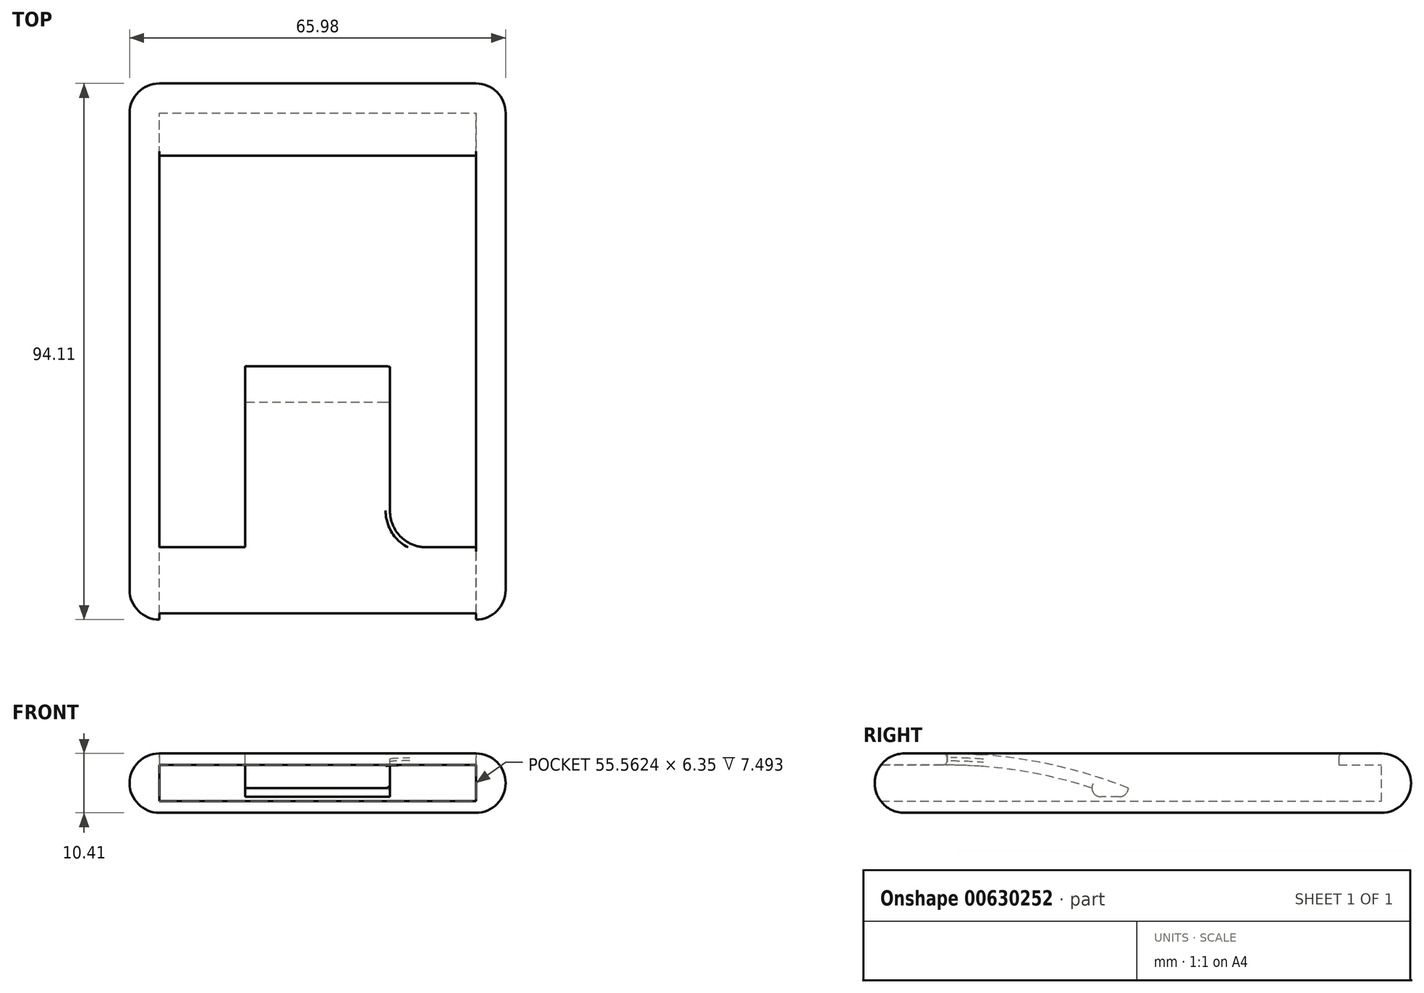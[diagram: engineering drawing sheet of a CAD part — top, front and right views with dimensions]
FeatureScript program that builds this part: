
annotation { "Feature Type Name" : "Feature", "Feature Type Description" : "" }
export const myFeature = defineFeature(function(context is Context, id is Id, definition is map)
    precondition{}
    {
        {
            var Q0;
            Q0=qCreatedBy(makeId("Front.planeOp"),FACE);
            var sketch = newSketch(context, id + "F0", { "sketchPlane" : qUnion([Q0])});
            skLineSegment(sketch, "E0.top", {"start": v(-27.78, 0) * mm, "end": v(27.78, 0) * mm});
            skLineSegment(sketch, "E0.left", {"start": v(-27.78, 2.03) * mm, "end": v(-27.78, 0) * mm});
            skLineSegment(sketch, "E0.right", {"start": v(27.78, 2.03) * mm, "end": v(27.78, 0) * mm});
            skLineSegment(sketch, "E1", {"start": v(0, 0) * mm, "end": v(0, 24.78) * mm, "construction": true});
            skLineSegment(sketch, "E2", {"start": v(-27.78, 2.03) * mm, "end": v(27.78, 2.03) * mm});
            skLineSegment(sketch, "E3", {"start": v(-27.78, 0) * mm, "end": v(-27.78, 10.41) * mm});
            skArc(sketch, "E4", {"start": v(-27.78, 10.41) * mm, "mid": v(-32.99, 5.2) * mm, "end": v(-27.78, 0) * mm});
            skLineSegment(sketch, "E5.MirrorCS", {"start": v(27.78, 0) * mm, "end": v(27.78, 10.41) * mm});
            skArc(sketch, "E6.MirrorCS", {"start": v(27.78, 10.41) * mm, "mid": v(32.99, 5.2) * mm, "end": v(27.78, 0) * mm});
            skSolve(sketch);
        }
        {
            var Q0;
            Q0 = qSketchRegion(id + "F0", true);
            extrude(context, id + "F1", {"entities" : qUnion([Q0]), "endBound" : BoundingType.SYMMETRIC, "depth" : 88.9 * mm, "offsetDistance" : 25.4 * mm});
        }
        {
            var Q0;
            Q0=makeQuery(id+"F1.opExtrude","CAP_FACE",FACE,{"disambiguationData":[OSD([sQuery(id+"F0.wireOp",EDGE,"E0.top"),sQuery(id+"F0.wireOp",EDGE,"E2"),sQuery(id+"F0.wireOp",EDGE,"E3"),sQuery(id+"F0.wireOp",EDGE,"E4"),sQuery(id+"F0.wireOp",EDGE,"E5.MirrorCS"),sQuery(id+"F0.wireOp",EDGE,"E6.MirrorCS")])],"isStart":true});
            var sketch = newSketch(context, id + "F2", { "sketchPlane" : qUnion([Q0])});
            skLineSegment(sketch, "E7", {"start": v(-27.78, 10.41) * mm, "end": v(27.78, 10.41) * mm});
            skSolve(sketch);
        }
        {
            var Q0;
            Q0 = qSketchRegion(id + "F2", true);
            var Q1;
            Q1=makeQuery(id+"F2.imprint","IMPRINT",FACE,{"disambiguationData":[TD([[makeQuery(id+"F2.imprint","IMPRINT",EDGE,{"derivedFrom":sQuery(id+"F2.wireOp",EDGE,"E7")}),-1.0]])]});
            var Q2;
            Q2=makeQuery(id+"F2.imprint","IMPRINT",FACE,{"disambiguationData":[TD([[makeQuery(id+"F2.imprint","IMPRINT",EDGE,{"derivedFrom":makeQuery(id+"F1.opExtrude","CAP_EDGE",EDGE,{"disambiguationData":[OSD([sQuery(id+"F0.wireOp",EDGE,"E0.top")])],"isStart":true})}),-1.0]])]});
            extrude(context, id + "F3", {"entities" : qUnion([Q0, Q1, Q2]), "operationType" : NewBodyOperationType.ADD, "depth" : 5.2 * mm, "offsetDistance" : 25.4 * mm});
        }
        {
            var Q0;
            Q0=makeQuery(id+"F1.opExtrude","SWEPT_FACE",FACE,{"disambiguationData":[OSD([sQuery(id+"F0.wireOp",EDGE,"E3")])]});
            var sketch = newSketch(context, id + "F4", { "sketchPlane" : qUnion([Q0])});
            skLineSegment(sketch, "E8.bottom", {"start": v(-44.45, 10.41) * mm, "end": v(-31.75, 10.41) * mm});
            skLineSegment(sketch, "E8.top", {"start": v(-44.45, 8.38) * mm, "end": v(-31.75, 8.38) * mm});
            skLineSegment(sketch, "E8.left", {"start": v(-44.45, 10.41) * mm, "end": v(-44.45, 8.38) * mm});
            skLineSegment(sketch, "E8.right", {"start": v(-31.75, 10.41) * mm, "end": v(-31.75, 8.38) * mm});
            skLineSegment(sketch, "E9.0", {"start": v(44.45, 2.03) * mm, "end": v(44.45, 10.41) * mm});
            skLineSegment(sketch, "E10", {"start": v(36.96, 10.41) * mm, "end": v(36.96, 8.38) * mm});
            skLineSegment(sketch, "E11.trimOffspring", {"start": v(36.96, 10.41) * mm, "end": v(44.45, 10.41) * mm});
            skLineSegment(sketch, "E12.trimOffspring", {"start": v(36.96, 8.38) * mm, "end": v(44.45, 8.38) * mm});
            skSolve(sketch);
        }
        {
            var Q0;
            Q0=makeQuery(id+"F4.imprint","IMPRINT",FACE,{"disambiguationData":[TD([[makeQuery(id+"F4.imprint","IMPRINT",EDGE,{"derivedFrom":sQuery(id+"F4.wireOp",EDGE,"E8.bottom")}),-1.0]])]});
            var Q1;
            Q1=makeQuery(id+"F4.imprint","IMPRINT",FACE,{"disambiguationData":[TD([[makeQuery(id+"F4.imprint","IMPRINT",EDGE,{"derivedFrom":sQuery(id+"F4.wireOp",EDGE,"E10")}),1.0]])]});
            extrude(context, id + "F5", {"entities" : qUnion([Q0, Q1]), "operationType" : NewBodyOperationType.ADD, "endBound" : BoundingType.UP_TO_NEXT, "depth" : 25.4 * mm, "offsetDistance" : 25.4 * mm});
        }
        {
            var Q0;
            Q0=makeQuery(id+"F3.opExtrude","CAP_EDGE",EDGE,{"disambiguationData":[OSD([sQuery(id+"F2.wireOp",EDGE,"E7")])],"isStart":false});
            var Q1;
            Q1=makeQuery(id+"F1.opExtrude","CAP_EDGE",EDGE,{"disambiguationData":[OSD([sQuery(id+"F0.wireOp",EDGE,"E4")])],"isStart":false});
            fillet(context, id + "F6", {"entities" : qUnion([Q0, Q1]), "radius" : 5.2 * mm, "tangentPropagation" : true, "allowEdgeOverflow" : false});
        }
        {
            var Q0;
            Q0=qCreatedBy(makeId("Right.planeOp"),FACE);
            var sketch = newSketch(context, id + "F7", { "sketchPlane" : qUnion([Q0])});
            skLineSegment(sketch, "E13.0", {"start": v(-31.75, 8.38) * mm, "end": v(-43.37, 8.38) * mm});
            skLineSegment(sketch, "E13.1", {"start": v(-31.75, 8.38) * mm, "end": v(-31.75, 10.41) * mm});
            skArc(sketch, "E14", {"start": v(0, 4.35) * mm, "mid": v(-15.59, 8.88) * mm, "end": v(-31.75, 10.41) * mm});
            skLineSegment(sketch, "E15", {"start": v(-1.52, 2.83) * mm, "end": v(-4.83, 2.83) * mm});
            skLineSegment(sketch, "E16", {"start": v(0, 4.35) * mm, "end": v(0, 4.35) * mm});
            skLineSegment(sketch, "E17", {"start": v(0, 4.35) * mm, "end": v(-6.35, 4.35) * mm, "construction": true});
            skLineSegment(sketch, "E18", {"start": v(-6.35, 4.35) * mm, "end": v(-6.35, 4.35) * mm});
            skArc(sketch, "E19", {"start": v(-6.35, 4.35) * mm, "mid": v(-18.9, 7.37) * mm, "end": v(-31.75, 8.38) * mm});
            skPoint(sketch, "E20.visualSharp", {"position": v(-6.35, 2.83) * mm});
            skArc(sketch, "E20.filletArc", {"start": v(-6.35, 4.35) * mm, "mid": v(-5.9, 3.27) * mm, "end": v(-4.83, 2.83) * mm});
            skPoint(sketch, "E21.visualSharp", {"position": v(0, 2.83) * mm});
            skArc(sketch, "E21.filletArc", {"start": v(-1.52, 2.83) * mm, "mid": v(-0.45, 3.27) * mm, "end": v(0, 4.35) * mm});
            skSolve(sketch);
        }
        {
            var Q0;
            Q0 = qSketchRegion(id + "F7", true);
            extrude(context, id + "F8", {"entities" : qUnion([Q0]), "operationType" : NewBodyOperationType.ADD, "endBound" : BoundingType.SYMMETRIC, "depth" : 25.4 * mm, "offsetDistance" : 25.4 * mm});
        }
        {
            var Q0;
            Q0=makeQuery(id+"F8.opExtrude","CAP_EDGE",EDGE,{"disambiguationData":[OSD([sQuery(id+"F7.wireOp",EDGE,"E13.1")])],"isStart":true});
            var Q1;
            Q1=makeQuery(id+"F5.opExtrude","CAP_EDGE",EDGE,{"disambiguationData":[OSD([sQuery(id+"F4.wireOp",EDGE,"E8.right")])],"isStart":true});
            var Q2;
            Q2=makeQuery(id+"F8.opExtrude","CAP_EDGE",EDGE,{"disambiguationData":[OSD([sQuery(id+"F7.wireOp",EDGE,"E13.1")])],"isStart":false});
            var Q3;
            Q3=makeQuery(id+"F5.opExtrude","CAP_EDGE",EDGE,{"disambiguationData":[OSD([sQuery(id+"F4.wireOp",EDGE,"E8.right")])],"isStart":false});
            var Q4;
            Q4=makeQuery(id+"F5.opExtrude","CAP_EDGE",EDGE,{"disambiguationData":[OSD([sQuery(id+"F4.wireOp",EDGE,"E10")])],"isStart":false});
            var Q5;
            Q5=makeQuery(id+"F5.opExtrude","CAP_EDGE",EDGE,{"disambiguationData":[OSD([sQuery(id+"F4.wireOp",EDGE,"E10")])],"isStart":true});
            fillet(context, id + "F9", {"entities" : qUnion([Q0, Q1, Q2, Q3, Q4, Q5]), "radius" : 6.35 * mm, "tangentPropagation" : true, "allowEdgeOverflow" : false});
        }
        {
            var Q0;
            Q0=makeQuery(id+"F9.opFillet","BLEND_EDGE",EDGE,{"blendedFrom":[makeQuery(id+"F8.opExtrude","CAP_EDGE",EDGE,{"disambiguationData":[OSD([sQuery(id+"F7.wireOp",EDGE,"E13.1")])],"isStart":false}),makeQuery(id+"F8.opExtrude","SWEPT_FACE",FACE,{"disambiguationData":[OSD([sQuery(id+"F7.wireOp",EDGE,"E14")])]})],"blendedInto":[makeQuery(id+"F8.opExtrude","SWEPT_FACE",FACE,{"disambiguationData":[OSD([sQuery(id+"F7.wireOp",EDGE,"E14")])]})]});
            var Q1;
            Q1=makeQuery(id+"F9.opFillet","BLEND_EDGE",EDGE,{"blendedFrom":[makeQuery(id+"F8.opExtrude","CAP_EDGE",EDGE,{"disambiguationData":[OSD([sQuery(id+"F7.wireOp",EDGE,"E13.1")])],"isStart":false}),makeQuery(id+"F8.opExtrude","SWEPT_FACE",FACE,{"disambiguationData":[OSD([sQuery(id+"F7.wireOp",EDGE,"E19")])]})],"blendedInto":[makeQuery(id+"F8.opExtrude","SWEPT_FACE",FACE,{"disambiguationData":[OSD([sQuery(id+"F7.wireOp",EDGE,"E19")])]})]});
            var Q2;
            Q2=makeQuery(id+"F9.opFillet","BLEND_EDGE",EDGE,{"blendedFrom":[makeQuery(id+"F8.opExtrude","CAP_EDGE",EDGE,{"disambiguationData":[OSD([sQuery(id+"F7.wireOp",EDGE,"E13.1")])],"isStart":true}),makeQuery(id+"F8.opExtrude","SWEPT_FACE",FACE,{"disambiguationData":[OSD([sQuery(id+"F7.wireOp",EDGE,"E14")])]})],"blendedInto":[makeQuery(id+"F8.opExtrude","SWEPT_FACE",FACE,{"disambiguationData":[OSD([sQuery(id+"F7.wireOp",EDGE,"E14")])]})]});
            var Q3;
            Q3=makeQuery(id+"F9.opFillet","BLEND_EDGE",EDGE,{"blendedFrom":[makeQuery(id+"F8.opExtrude","CAP_EDGE",EDGE,{"disambiguationData":[OSD([sQuery(id+"F7.wireOp",EDGE,"E13.1")])],"isStart":true}),makeQuery(id+"F8.opExtrude","SWEPT_FACE",FACE,{"disambiguationData":[OSD([sQuery(id+"F7.wireOp",EDGE,"E19")])]})],"blendedInto":[makeQuery(id+"F8.opExtrude","SWEPT_FACE",FACE,{"disambiguationData":[OSD([sQuery(id+"F7.wireOp",EDGE,"E19")])]})]});
            var Q4;
            Q4=makeQuery(id+"F5.opExtrude","SWEPT_EDGE",EDGE,{"disambiguationData":[OSD([sQuery(id+"F0.wireOp",EDGE,"E3"),sQuery(id+"F0.wireOp",EDGE,"E4"),sQuery(id+"F4.wireOp",EDGE,"E10"),sQuery(id+"F4.wireOp",EDGE,"E11.trimOffspring")])]});
            fillet(context, id + "F10", {"entities" : qUnion([Q0, Q1, Q2, Q3, Q4]), "radius" : 0.76 * mm, "tangentPropagation" : true, "allowEdgeOverflow" : false});
        }
    });
